# Revit family: Receptor_Sani-Flor_12-In_Square_8-In_Sump_Zurn-Z1751
name_source: partatom
category: Plumbing Fixtures
units: mm (PartAtom-declared; Revit-internal decimal feet)

## family parameters
Always vertical = Yes
Cut with Voids When Loaded = No
Maintain Annotation Orientation = No
OmniClass Number = 23.45.05.14.14
OmniClass Title = Sinks/Lavatories
Part Type = Normal
Room Calculation Point = No
Round Connector Dimension = Use Radius
Shared = No
Work Plane-Based = No

## types (18) — shared parameters
Assembly Code = D2030300
CW Connection = No
Default Elevation = 4 "
Description = 12 X 12 [305 X 305] SANI-FLOR RECEPTOR 8 [203] SUMP DEPTH
Grate Open Area (Sq. In) = 23
HW Connection = No
Manufacturer = Zurn Water, LLC
Manufacurer Brand = Zurn
Modified Date = 09/24/2025
Product Documentation Link = https://files.zurn.com
Product Page URL = https://www.zurn.com
Product data url = https://www.bimobject.com
Thickness = 0.063 "
Trap Primer = Yes
URL = www.zurn.com
Vent Connection = No
Waste Connection = Yes
zero-valued in all types: CWFU, HWFU, WFU

## per-type parameters (varying)
| type | A_ Pipe Size (Actual-Inner) | A_ Pipe Size (Actual-Outer) | A_ Pipe Size (Nominal) | Approx. Weight (Lbs) | Connector Radius | E_ Body Length | Main Material | Type Comments |
| Z1751-3NH | 2.998 " | 3.5 " | 3 " | 19 " | 1.5 " | 10.063 " | Steel - Zurn - Stainless - Type 304 | Z1751 Sani-Flor Receptor 3 Inch No-Hub Outlet |
| Z1751-2NH | 2.067 " | 2.375 " | 2 " | 19 " | 1 " | 10.063 " | Steel - Zurn - Stainless - Type 304 | Z1751 Sani-Flor Receptor 2 Inch No-Hub Outlet |
| Z1751-4NH | 4.026 " | 4.5 " | 4 " | 19 " | 2 " | 10.063 " | Steel - Zurn - Stainless - Type 304 | Z1751 Sani-Flor Receptor 4 Inch No-Hub Outlet |
| Z1751-6NH | 6.065 " | 6.625 " | 6 " | 21 " | 3 " | 10.063 " | Steel - Zurn - Stainless - Type 304 | Z1751 Sani-Flor Receptor 6 Inch No-Hub Outlet |
| Z1751-3IC | 2.998 " | 3.5 " | 3 " | 19 " | 1.5 " | 10.563 " | Steel - Zurn - Stainless - Type 304 | Z1751 Sani-Flor Receptor 3 Inch Inside Caulk Outlet |
| Z1751-4IC | 4.026 " | 4.5 " | 4 " | 19 " | 2 " | 10.563 " | Steel - Zurn - Stainless - Type 304 | Z1751 Sani-Flor Receptor 4 Inch Inside Caulk Outlet |
| Z1751-2NL | 2.067 " | 2.375 " | 2 " | 19 " | 1 " | 9.813 " | Steel - Zurn - Stainless - Type 304 | Z1751 Sani-Flor Receptor 2 Inch Neo-Loc Outlet |
| Z1751-3NL | 2.998 " | 3.5 " | 3 " | 19 " | 1.5 " | 9.813 " | Steel - Zurn - Stainless - Type 304 | Z1751 Sani-Flor Receptor 3 Inch Neo-Loc Outlet |
| Z1751-4NL | 4.026 " | 4.5 " | 4 " | 19 " | 2 " | 9.813 " | Steel - Zurn - Stainless - Type 304 | Z1751 Sani-Flor Receptor 4 Inch Neo-Loc Outlet |
| ZM1751-3NH | 2.998 " | 3.5 " | 3 " | 19 " | 1.5 " | 10.063 " | Steel - Zurn - Stainless - Type 316 | ZM1751 Sani-Flor Receptor 3 Inch No-Hub Outlet |
| ZM1751-2NH | 2.067 " | 2.375 " | 2 " | 19 " | 1 " | 10.063 " | Steel - Zurn - Stainless - Type 316 | ZM1751 Sani-Flor Receptor 2 Inch No-Hub Outlet |
| ZM1751-4NH | 4.026 " | 4.5 " | 4 " | 19 " | 2 " | 10.063 " | Steel - Zurn - Stainless - Type 316 | ZM1751 Sani-Flor Receptor 4 Inch No-Hub Outlet |
| ZM1751-6NH | 6.065 " | 6.625 " | 6 " | 21 " | 3 " | 10.063 " | Steel - Zurn - Stainless - Type 316 | ZM1751 Sani-Flor Receptor 6 Inch No-Hub Outlet |
| ZM1751-3IC | 2.998 " | 3.5 " | 3 " | 19 " | 1.5 " | 10.563 " | Steel - Zurn - Stainless - Type 316 | ZM1751 Sani-Flor Receptor 3 Inch Inside Caulk Outlet |
| ZM1751-4IC | 4.026 " | 4.5 " | 4 " | 19 " | 2 " | 10.563 " | Steel - Zurn - Stainless - Type 316 | ZM1751 Sani-Flor Receptor 4 Inch Inside Caulk Outlet |
| ZM1751-2NL | 2.067 " | 2.375 " | 2 " | 19 " | 1 " | 9.813 " | Steel - Zurn - Stainless - Type 316 | ZM1751 Sani-Flor Receptor 2 Inch Neo-Loc Outlet |
| ZM1751-3NL | 2.998 " | 3.5 " | 3 " | 19 " | 1.5 " | 9.813 " | Steel - Zurn - Stainless - Type 316 | ZM1751 Sani-Flor Receptor 3 Inch Neo-Loc Outlet |
| ZM1751-4NL | 4.026 " | 4.5 " | 4 " | 19 " | 2 " | 9.813 " | Steel - Zurn - Stainless - Type 316 | ZM1751 Sani-Flor Receptor 4 Inch Neo-Loc Outlet |

note: column(s) folded — value = type name in every type: Model

## geometry (parser evidence)
native form markers: Blend x8, Sweep x6
no freeform markers — native parametric forms only
